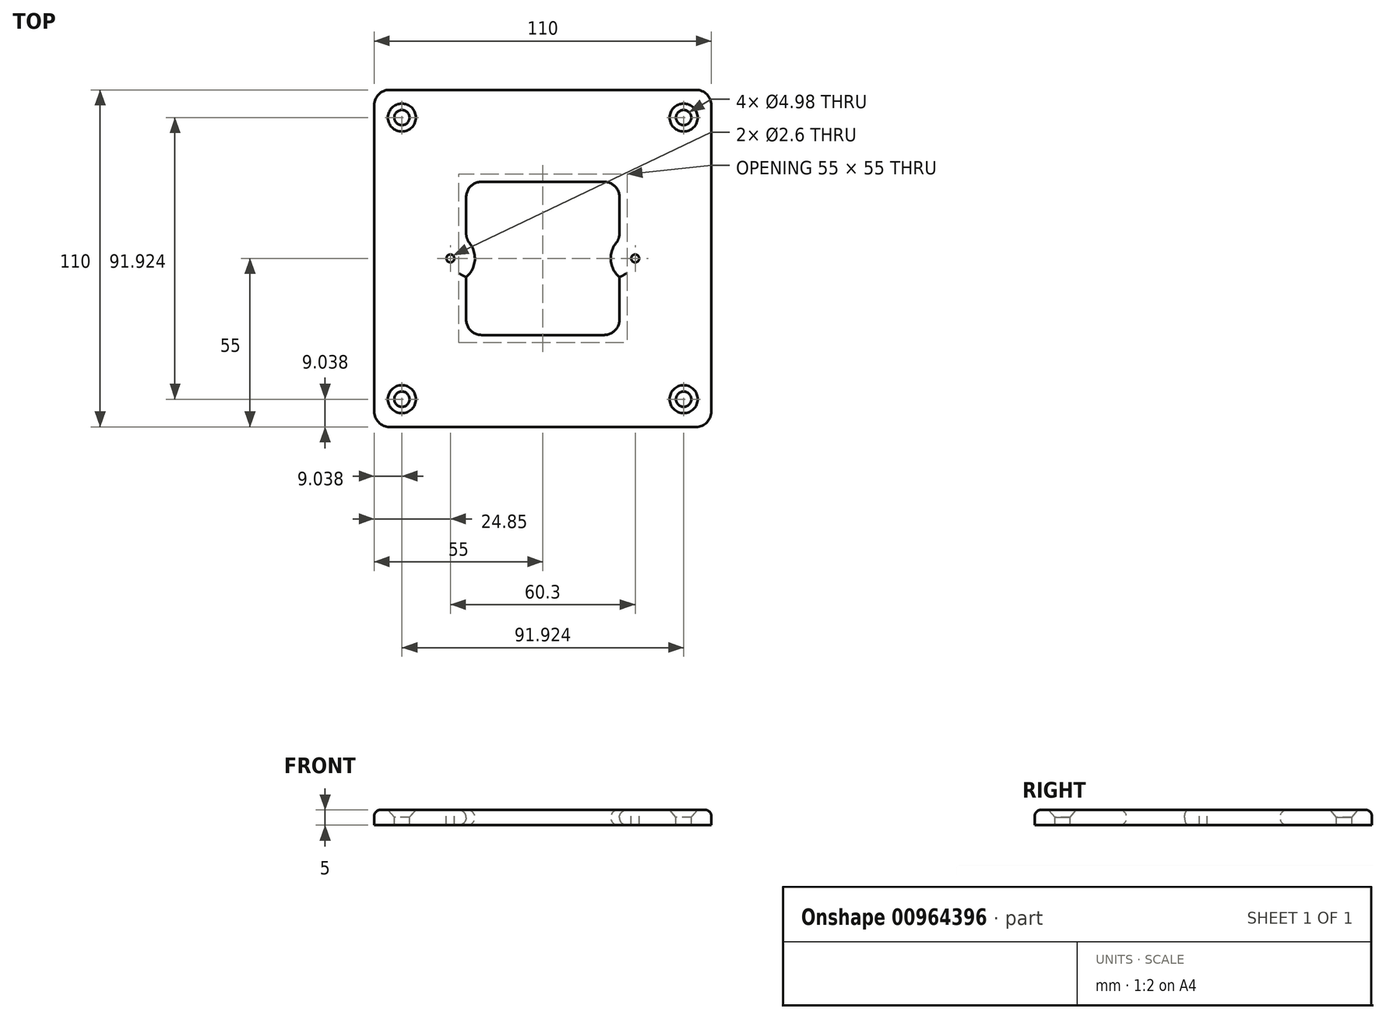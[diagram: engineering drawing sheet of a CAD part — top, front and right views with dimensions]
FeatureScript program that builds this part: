
annotation { "Feature Type Name" : "Feature", "Feature Type Description" : "" }
export const myFeature = defineFeature(function(context is Context, id is Id, definition is map)
    precondition{}
    {
        {
            var Q0;
            Q0=qCreatedBy(makeId("Top.planeOp"),FACE);
            var sketch = newSketch(context, id + "F0", { "sketchPlane" : qUnion([Q0])});
            skLineSegment(sketch, "E0.bottom", {"start": v(25, 25) * mm, "end": v(-25, 25) * mm});
            skLineSegment(sketch, "E0.top", {"start": v(25, -25) * mm, "end": v(-25, -25) * mm});
            skLineSegment(sketch, "E0.left", {"start": v(25, 25) * mm, "end": v(25, 6.12) * mm});
            skLineSegment(sketch, "E0.right", {"start": v(-25, 25) * mm, "end": v(-25, 6.12) * mm});
            skPoint(sketch, "E0.middle", {"position": v(0, 0) * mm});
            skLineSegment(sketch, "E1.bottom", {"start": v(55, 55) * mm, "end": v(-55, 55) * mm});
            skLineSegment(sketch, "E1.top", {"start": v(55, -55) * mm, "end": v(-55, -55) * mm});
            skLineSegment(sketch, "E1.left", {"start": v(55, 55) * mm, "end": v(55, -55) * mm});
            skLineSegment(sketch, "E1.right", {"start": v(-55, 55) * mm, "end": v(-55, -55) * mm});
            skLineSegment(sketch, "E2", {"start": v(-55, 0) * mm, "end": v(-25, 0) * mm, "construction": true});
            skLineSegment(sketch, "E3", {"start": v(-55, 55) * mm, "end": v(-25, 25) * mm, "construction": true});
            skLineSegment(sketch, "E4", {"start": v(25, 25) * mm, "end": v(55, 55) * mm, "construction": true});
            skLineSegment(sketch, "E5", {"start": v(25, -25) * mm, "end": v(55, -55) * mm, "construction": true});
            skLineSegment(sketch, "E6", {"start": v(-25, -25) * mm, "end": v(-55, -55) * mm, "construction": true});
            skPoint(sketch, "E7", {"position": v(-45.96, 45.96) * mm});
            skPoint(sketch, "E8", {"position": v(45.96, 45.96) * mm});
            skPoint(sketch, "E9", {"position": v(45.96, -45.96) * mm});
            skPoint(sketch, "E10", {"position": v(-45.96, -45.96) * mm});
            skLineSegment(sketch, "E11", {"start": v(25, 0) * mm, "end": v(55, 0) * mm, "construction": true});
            skPoint(sketch, "E12", {"position": v(-30.15, 0) * mm});
            skCircle(sketch, "E13", {"center": v(0, 0) * mm, "radius": 30.15 * mm, "construction": true});
            skPoint(sketch, "E14", {"position": v(30.15, 0) * mm});
            skCircle(sketch, "E15", {"center": v(0, 0) * mm, "radius": 65 * mm});
            skArc(sketch, "E16", {"start": v(-25, -6.12) * mm, "mid": v(-22.15, 0) * mm, "end": v(-25, 6.12) * mm});
            skArc(sketch, "E17", {"start": v(25, 6.12) * mm, "mid": v(22.15, 0) * mm, "end": v(25, -6.12) * mm});
            skLineSegment(sketch, "E18.trimOffspring", {"start": v(25, -6.12) * mm, "end": v(25, -25) * mm});
            skLineSegment(sketch, "E19.trimOffspring", {"start": v(-25, -6.12) * mm, "end": v(-25, -25) * mm});
            skSolve(sketch);
        }
        {
            var Q0;
            Q0=makeQuery(id+"F0.imprint","IMPRINT",FACE,{"disambiguationData":[TD([[makeQuery(id+"F0.imprint","IMPRINT",EDGE,{"derivedFrom":sQuery(id+"F0.wireOp",EDGE,"E0.bottom")}),-1.0]])]});
            var Q1;
            {var subQ0=sQuery(id+"F0.wireOp",EDGE,"E1.right");var subQ1=sQuery(id+"F0.wireOp",EDGE,"E1.top");var subQ2=makeQuery(id+"F0.imprint","INTERSECT",VERTEX,{"derivedFrom":[subQ1,subQ0]});Q1=makeQuery(id+"F0.imprint","IMPRINT",FACE,{"disambiguationData":[TD([[makeQuery(id+"F0.imprint","IMPRINT",EDGE,{"disambiguationData":[TD([[subQ2,1.0]])],"derivedFrom":subQ1}),-1.0]])]});}
            var Q2;
            {var subQ0=sQuery(id+"F0.wireOp",EDGE,"E1.right");var subQ1=sQuery(id+"F0.wireOp",EDGE,"E1.bottom");var subQ2=makeQuery(id+"F0.imprint","INTERSECT",VERTEX,{"derivedFrom":[subQ1,subQ0]});Q2=makeQuery(id+"F0.imprint","IMPRINT",FACE,{"disambiguationData":[TD([[makeQuery(id+"F0.imprint","IMPRINT",EDGE,{"disambiguationData":[TD([[subQ2,1.0]])],"derivedFrom":subQ1}),1.0]])]});}
            var Q3;
            {var subQ0=sQuery(id+"F0.wireOp",EDGE,"E1.left");var subQ1=sQuery(id+"F0.wireOp",EDGE,"E1.bottom");var subQ2=makeQuery(id+"F0.imprint","INTERSECT",VERTEX,{"derivedFrom":[subQ1,subQ0]});Q3=makeQuery(id+"F0.imprint","IMPRINT",FACE,{"disambiguationData":[TD([[makeQuery(id+"F0.imprint","IMPRINT",EDGE,{"disambiguationData":[TD([[subQ2,-1.0]])],"derivedFrom":subQ1}),1.0]])]});}
            var Q4;
            {var subQ0=sQuery(id+"F0.wireOp",EDGE,"E1.left");var subQ1=sQuery(id+"F0.wireOp",EDGE,"E1.top");var subQ2=makeQuery(id+"F0.imprint","INTERSECT",VERTEX,{"derivedFrom":[subQ1,subQ0]});Q4=makeQuery(id+"F0.imprint","IMPRINT",FACE,{"disambiguationData":[TD([[makeQuery(id+"F0.imprint","IMPRINT",EDGE,{"disambiguationData":[TD([[subQ2,-1.0]])],"derivedFrom":subQ1}),-1.0]])]});}
            extrude(context, id + "F1", {"entities" : qUnion([Q0, Q1, Q2, Q3, Q4]), "oppositeDirection" : true, "depth" : 5 * mm, "offsetDistance" : 25 * mm});
        }
        {
            var Q0;
            Q0=makeQuery(id+"F1.opExtrude","SWEPT_EDGE",EDGE,{"disambiguationData":[OSD([sQuery(id+"F0.wireOp",EDGE,"E1.top"),sQuery(id+"F0.wireOp",EDGE,"E1.right")])]});
            var Q1;
            Q1=makeQuery(id+"F1.opExtrude","SWEPT_EDGE",EDGE,{"disambiguationData":[OSD([sQuery(id+"F0.wireOp",EDGE,"E1.top"),sQuery(id+"F0.wireOp",EDGE,"E1.left")])]});
            var Q2;
            Q2=makeQuery(id+"F1.opExtrude","SWEPT_EDGE",EDGE,{"disambiguationData":[OSD([sQuery(id+"F0.wireOp",EDGE,"E1.bottom"),sQuery(id+"F0.wireOp",EDGE,"E1.left")])]});
            var Q3;
            Q3=makeQuery(id+"F1.opExtrude","SWEPT_EDGE",EDGE,{"disambiguationData":[OSD([sQuery(id+"F0.wireOp",EDGE,"E1.bottom"),sQuery(id+"F0.wireOp",EDGE,"E1.right")])]});
            fillet(context, id + "F2", {"entities" : qUnion([Q0, Q1, Q2, Q3]), "radius" : 5 * mm, "tangentPropagation" : true, "allowEdgeOverflow" : false});
        }
        {
            var Q0;
            Q0=sQuery(id+"F0.wireOp",VERTEX,"E9");
            var Q1;
            Q1=sQuery(id+"F0.wireOp",VERTEX,"E10");
            var Q2;
            Q2=sQuery(id+"F0.wireOp",VERTEX,"E7");
            var Q3;
            Q3=sQuery(id+"F0.wireOp",VERTEX,"E8");
            var Q4;
            Q4=makeQuery(id+"F1.opExtrude","SWEPT_BODY",BODY,{"disambiguationData":[OSD([sQuery(id+"F0.wireOp",EDGE,"E0.bottom"),sQuery(id+"F0.wireOp",EDGE,"E0.top"),sQuery(id+"F0.wireOp",EDGE,"E0.left"),sQuery(id+"F0.wireOp",EDGE,"E0.right"),sQuery(id+"F0.wireOp",EDGE,"E1.bottom"),sQuery(id+"F0.wireOp",EDGE,"E1.top"),sQuery(id+"F0.wireOp",EDGE,"E1.left"),sQuery(id+"F0.wireOp",EDGE,"E1.right")])]});
            hole(context, id + "F3", {"style" : HoleStyle.C_SINK, "endStyle" : HoleEndStyle.BLIND, "standardTappedOrClearance" : lookupTablePath({ "fit" : "Normal (ASME)", "standard" : "ANSI", "size" : "#8", "type" : "Clearance" }), "standardBlindInLast" : lookupTablePath({ "fit" : "Normal", "standard" : "ANSI", "engagement" : "75%", "pitch" : "32 tpi", "size" : "#8", "type" : "Clearance & tapped" }), "holeDiameter" : 4.98 * mm, "cSinkDiameter" : 9.12 * mm, "cSinkAngle" : 82 * degree, "majorDiameter" : 5 * mm, "holeDepth" : 15 * mm, "isTappedThrough" : true, "tappedDepth" : 13.5 * mm, "tapClearance" : 3, "startFromSketch" : true, "locations" : qUnion([Q0, Q1, Q2, Q3]), "scope" : qUnion([Q4])});
        }
        {
            var Q0;
            Q0=sQuery(id+"F0.wireOp",VERTEX,"E14");
            var Q1;
            Q1=sQuery(id+"F0.wireOp",VERTEX,"E12");
            var Q2;
            Q2=makeQuery(id+"F1.opExtrude","SWEPT_BODY",BODY,{"disambiguationData":[OSD([sQuery(id+"F0.wireOp",EDGE,"E0.bottom"),sQuery(id+"F0.wireOp",EDGE,"E0.top"),sQuery(id+"F0.wireOp",EDGE,"E0.left"),sQuery(id+"F0.wireOp",EDGE,"E0.right"),sQuery(id+"F0.wireOp",EDGE,"E1.bottom"),sQuery(id+"F0.wireOp",EDGE,"E1.top"),sQuery(id+"F0.wireOp",EDGE,"E1.left"),sQuery(id+"F0.wireOp",EDGE,"E1.right")])]});
            hole(context, id + "F4", {"style" : HoleStyle.SIMPLE, "endStyle" : HoleEndStyle.BLIND, "standardTappedOrClearance" : lookupTablePath({ "fit" : "Normal", "standard" : "ISO", "size" : "M2.2", "type" : "Clearance" }), "standardBlindInLast" : lookupTablePath({ "fit" : "Normal", "standard" : "ISO", "engagement" : "75%", "pitch" : "0.25 mm", "size" : "M2.2", "type" : "Clearance & tapped" }), "holeDiameter" : 2.6 * mm, "majorDiameter" : 5 * mm, "holeDepth" : 15 * mm, "isTappedThrough" : true, "tappedDepth" : 13.5 * mm, "tapClearance" : 3, "startFromSketch" : true, "locations" : qUnion([Q0, Q1]), "scope" : qUnion([Q2])});
        }
        {
            var Q0;
            Q0=makeQuery(id+"F1.opExtrude","SWEPT_EDGE",EDGE,{"disambiguationData":[OSD([sQuery(id+"F0.wireOp",EDGE,"E0.top"),sQuery(id+"F0.wireOp",EDGE,"E0.right")])]});
            var Q1;
            Q1=makeQuery(id+"F1.opExtrude","SWEPT_EDGE",EDGE,{"disambiguationData":[OSD([sQuery(id+"F0.wireOp",EDGE,"E0.top"),sQuery(id+"F0.wireOp",EDGE,"E0.left")])]});
            var Q2;
            Q2=makeQuery(id+"F1.opExtrude","SWEPT_EDGE",EDGE,{"disambiguationData":[OSD([sQuery(id+"F0.wireOp",EDGE,"E0.bottom"),sQuery(id+"F0.wireOp",EDGE,"E0.right")])]});
            var Q3;
            Q3=makeQuery(id+"F1.opExtrude","SWEPT_EDGE",EDGE,{"disambiguationData":[OSD([sQuery(id+"F0.wireOp",EDGE,"E0.bottom"),sQuery(id+"F0.wireOp",EDGE,"E0.left")])]});
            fillet(context, id + "F5", {"entities" : qUnion([Q0, Q1, Q2, Q3]), "radius" : 5 * mm, "tangentPropagation" : true, "allowEdgeOverflow" : false});
        }
        {
            var Q0;
            Q0=makeQuery(id+"F1.opExtrude","CAP_EDGE",EDGE,{"disambiguationData":[OSD([sQuery(id+"F0.wireOp",EDGE,"E1.left")])],"isStart":true});
            fillet(context, id + "F6", {"entities" : qUnion([Q0]), "radius" : 2 * mm, "tangentPropagation" : true, "allowEdgeOverflow" : false});
        }
        {
            var Q0;
            Q0=makeQuery(id+"F1.opExtrude","CAP_EDGE",EDGE,{"disambiguationData":[OSD([sQuery(id+"F0.wireOp",EDGE,"E0.bottom")])],"isStart":false});
            var Q1;
            Q1=makeQuery(id+"F1.opExtrude","CAP_EDGE",EDGE,{"disambiguationData":[OSD([sQuery(id+"F0.wireOp",EDGE,"E0.top")])],"isStart":true});
            var Q2;
            Q2=makeQuery(id+"F1.opExtrude","CAP_EDGE",EDGE,{"disambiguationData":[OSD([sQuery(id+"F0.wireOp",EDGE,"E18.trimOffspring")])],"isStart":false});
            var Q3;
            Q3=makeQuery(id+"F1.opExtrude","CAP_EDGE",EDGE,{"disambiguationData":[OSD([sQuery(id+"F0.wireOp",EDGE,"E16")])],"isStart":true});
            fillet(context, id + "F7", {"entities" : qUnion([Q0, Q1, Q2, Q3]), "radius" : 2.5 * mm, "tangentPropagation" : true, "allowEdgeOverflow" : false});
        }
    });
